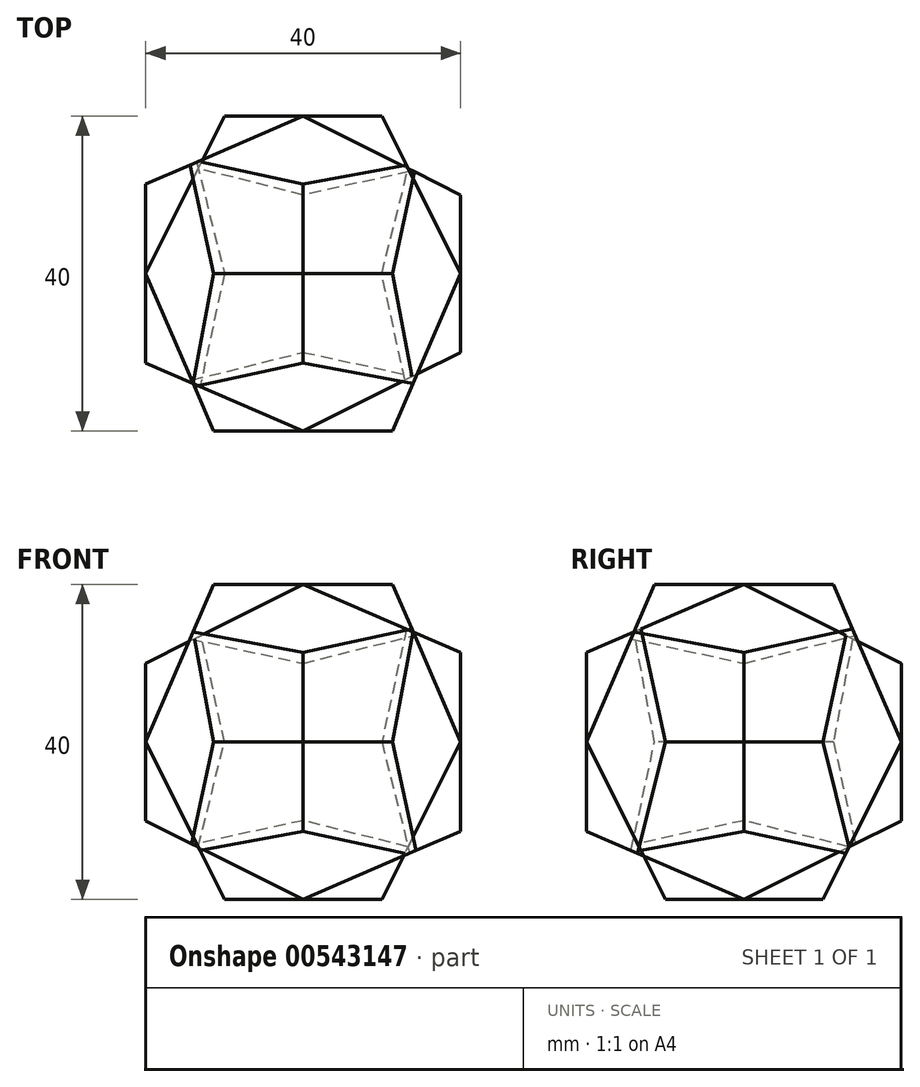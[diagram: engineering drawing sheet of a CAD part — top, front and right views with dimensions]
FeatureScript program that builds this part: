
annotation { "Feature Type Name" : "Feature", "Feature Type Description" : "" }
export const myFeature = defineFeature(function(context is Context, id is Id, definition is map)
    precondition{}
    {
        {
            var Q0;
            Q0=qCreatedBy(makeId("Front.planeOp"),FACE);
            var sketch = newSketch(context, id + "F0", { "sketchPlane" : qUnion([Q0])});
            skLineSegment(sketch, "E0", {"start": v(46.28, 0) * mm, "end": v(0, 20) * mm});
            skLineSegment(sketch, "E1", {"start": v(0, 20) * mm, "end": v(-40, 0) * mm});
            skLineSegment(sketch, "E2", {"start": v(-40, 0) * mm, "end": v(0, -20) * mm});
            skLineSegment(sketch, "E3", {"start": v(0, -20) * mm, "end": v(46.28, 0) * mm});
            skSolve(sketch);
        }
        {
            var Q0;
            Q0=makeQuery(id+"F0.imprint","IMPRINT",FACE,{"disambiguationData":[TD([[makeQuery(id+"F0.imprint","IMPRINT",EDGE,{"derivedFrom":sQuery(id+"F0.wireOp",EDGE,"E0")}),1.0]])]});
            extrude(context, id + "F1", {"entities" : qUnion([Q0]), "depth" : 25 * mm, "offsetDistance" : 25 * mm, "hasSecondDirection" : true, "secondDirectionOppositeDirection" : true, "secondDirectionDepth" : 25 * mm});
        }
        {
            var Q0;
            Q0=qCreatedBy(makeId("Front.planeOp"),FACE);
            var sketch = newSketch(context, id + "F2", { "sketchPlane" : qUnion([Q0])});
            skLineSegment(sketch, "E4", {"start": v(0, 49.78) * mm, "end": v(0, 0) * mm});
            skSolve(sketch);
        }
        {
            var Q0;
            Q0=qCreatedBy(makeId("Front.planeOp"),FACE);
            var sketch = newSketch(context, id + "F3", { "sketchPlane" : qUnion([Q0])});
            skLineSegment(sketch, "E5", {"start": v(60.84, 0) * mm, "end": v(0, 0) * mm});
            skSolve(sketch);
        }
        {
            var Q0;
            Q0=qCreatedBy(makeId("Right.planeOp"),FACE);
            var sketch = newSketch(context, id + "F4", { "sketchPlane" : qUnion([Q0])});
            skLineSegment(sketch, "E6", {"start": v(48.72, 0) * mm, "end": v(-1.84, 0) * mm});
            skSolve(sketch);
        }
        {
            var Q0;
            Q0=makeQuery(id+"F1.opExtrude","SWEPT_BODY",BODY,{"disambiguationData":[OSD([sQuery(id+"F0.wireOp",EDGE,"E0"),sQuery(id+"F0.wireOp",EDGE,"E1"),sQuery(id+"F0.wireOp",EDGE,"E2"),sQuery(id+"F0.wireOp",EDGE,"E3")])]});
            var Q1;
            Q1=sQuery(id+"F2.wireOp",EDGE,"E4");
            transform(context, id + "F5", {"entities" : qUnion([Q0]), "transformType" : TransformType.ROTATION, "transformAxis" : qUnion([Q1]), "angle" : 90 * degree, "makeCopy" : true});
        }
        {
            var Q0;
            Q0=makeQuery(id+"F5.opPattern","COPY",BODY,{"derivedFrom":makeQuery(id+"F1.opExtrude","SWEPT_BODY",BODY,{"disambiguationData":[OSD([sQuery(id+"F0.wireOp",EDGE,"E0"),sQuery(id+"F0.wireOp",EDGE,"E1"),sQuery(id+"F0.wireOp",EDGE,"E2"),sQuery(id+"F0.wireOp",EDGE,"E3")])]}),"instanceName":"1"});
            var Q1;
            Q1=sQuery(id+"F4.wireOp",EDGE,"E6");
            transform(context, id + "F6", {"entities" : qUnion([Q0]), "transformType" : TransformType.ROTATION, "transformAxis" : qUnion([Q1]), "angle" : 90 * degree, "makeCopy" : true});
        }
        {
            var Q0;
            Q0=makeQuery(id+"F5.opPattern","COPY",BODY,{"derivedFrom":makeQuery(id+"F1.opExtrude","SWEPT_BODY",BODY,{"disambiguationData":[OSD([sQuery(id+"F0.wireOp",EDGE,"E0"),sQuery(id+"F0.wireOp",EDGE,"E1"),sQuery(id+"F0.wireOp",EDGE,"E2"),sQuery(id+"F0.wireOp",EDGE,"E3")])]}),"instanceName":"1"});
            var Q1;
            Q1=sQuery(id+"F3.wireOp",EDGE,"E5");
            transform(context, id + "F7", {"entities" : qUnion([Q0]), "transformType" : TransformType.ROTATION, "transformAxis" : qUnion([Q1]), "angle" : 90 * degree, "makeCopy" : false});
        }
        {
            var Q0;
            Q0=makeQuery(id+"F5.opPattern","COPY",BODY,{"derivedFrom":makeQuery(id+"F1.opExtrude","SWEPT_BODY",BODY,{"disambiguationData":[OSD([sQuery(id+"F0.wireOp",EDGE,"E0"),sQuery(id+"F0.wireOp",EDGE,"E1"),sQuery(id+"F0.wireOp",EDGE,"E2"),sQuery(id+"F0.wireOp",EDGE,"E3")])]}),"instanceName":"1"});
            var Q1;
            Q1=makeQuery(id+"F6.opPattern","COPY",BODY,{"derivedFrom":makeQuery(id+"F5.opPattern","COPY",BODY,{"derivedFrom":makeQuery(id+"F1.opExtrude","SWEPT_BODY",BODY,{"disambiguationData":[OSD([sQuery(id+"F0.wireOp",EDGE,"E0"),sQuery(id+"F0.wireOp",EDGE,"E1"),sQuery(id+"F0.wireOp",EDGE,"E2"),sQuery(id+"F0.wireOp",EDGE,"E3")])]}),"instanceName":"1"}),"instanceName":"1"});
            booleanBodies(context, id + "F8", {"operationType" : BooleanOperationType.INTERSECTION, "tools" : qUnion([Q0, Q1])});
        }
        {
            var Q0;
            {var subQ0=makeQuery(id+"F5.opPattern","COPY",BODY,{"derivedFrom":makeQuery(id+"F1.opExtrude","SWEPT_BODY",BODY,{"disambiguationData":[OSD([sQuery(id+"F0.wireOp",EDGE,"E0"),sQuery(id+"F0.wireOp",EDGE,"E1"),sQuery(id+"F0.wireOp",EDGE,"E2"),sQuery(id+"F0.wireOp",EDGE,"E3")])]}),"instanceName":"1"});Q0=makeQuery(id+"F8.opBoolean","INTERSECT",BODY,{"derivedFrom":[subQ0,makeQuery(id+"F6.opPattern","COPY",BODY,{"derivedFrom":subQ0,"instanceName":"1"})]});}
            var Q1;
            Q1=makeQuery(id+"F1.opExtrude","SWEPT_BODY",BODY,{"disambiguationData":[OSD([sQuery(id+"F0.wireOp",EDGE,"E0"),sQuery(id+"F0.wireOp",EDGE,"E1"),sQuery(id+"F0.wireOp",EDGE,"E2"),sQuery(id+"F0.wireOp",EDGE,"E3")])]});
            booleanBodies(context, id + "F9", {"operationType" : BooleanOperationType.INTERSECTION, "tools" : qUnion([Q0, Q1])});
        }
        {
            var Q0;
            {var subQ0=makeQuery(id+"F1.opExtrude","SWEPT_BODY",BODY,{"disambiguationData":[OSD([sQuery(id+"F0.wireOp",EDGE,"E0"),sQuery(id+"F0.wireOp",EDGE,"E1"),sQuery(id+"F0.wireOp",EDGE,"E2"),sQuery(id+"F0.wireOp",EDGE,"E3")])]});var subQ1=makeQuery(id+"F5.opPattern","COPY",BODY,{"derivedFrom":subQ0,"instanceName":"1"});Q0=makeQuery(id+"F9.opBoolean","INTERSECT",BODY,{"derivedFrom":[subQ0,makeQuery(id+"F8.opBoolean","INTERSECT",BODY,{"derivedFrom":[subQ1,makeQuery(id+"F6.opPattern","COPY",BODY,{"derivedFrom":subQ1,"instanceName":"1"})]})]});}
            var Q1;
            Q1=sQuery(id+"F2.wireOp",EDGE,"E4");
            transform(context, id + "F10", {"entities" : qUnion([Q0]), "transformType" : TransformType.ROTATION, "transformAxis" : qUnion([Q1]), "angle" : 90 * degree, "makeCopy" : true});
        }
    });
